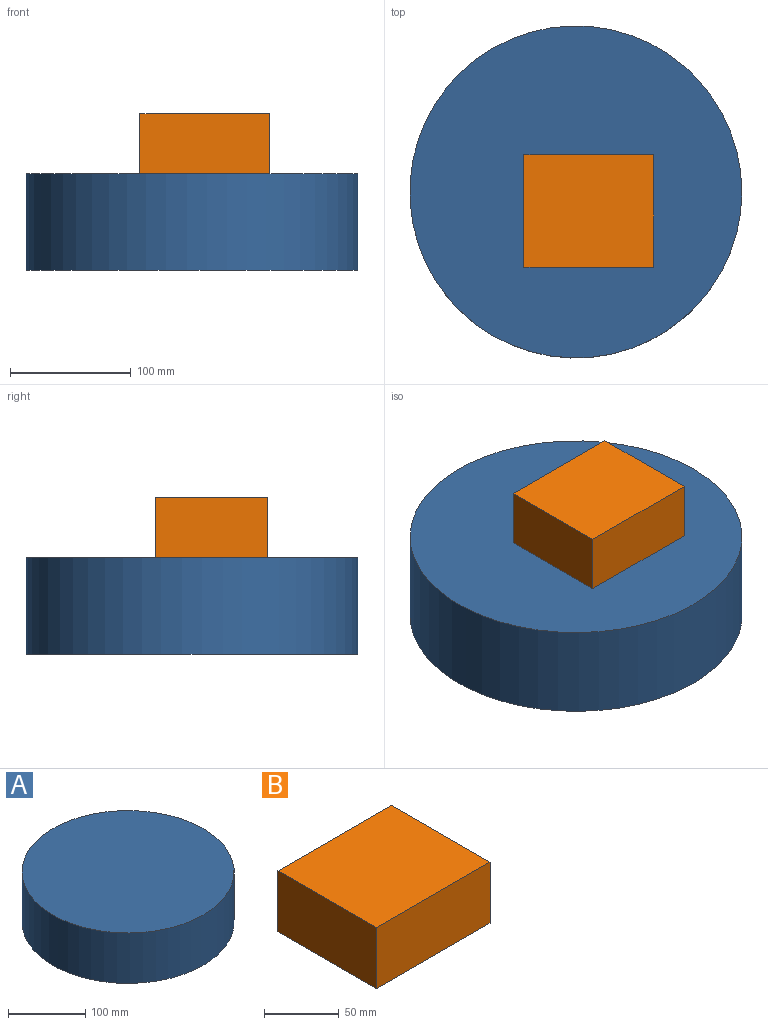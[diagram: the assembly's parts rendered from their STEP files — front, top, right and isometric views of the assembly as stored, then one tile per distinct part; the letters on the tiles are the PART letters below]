
ASSEMBLY  parts=2 mates=1
PART A: 3 faces, bbox 275.2x275.2x80 mm
  f0: cylinder r=137.62mm len=275.23mm, axis (0,0,1), area 69173.8mm2, adj f1,f2
  f1: plane 275.23x275.23mm, normal (0,0,-1), area 59496.8mm2, adj f0
  f2: plane 275.23x275.23mm, normal (0,0,1), area 59496.8mm2, adj f0
PART B: 6 faces, bbox 107.4x93.1x50 mm
  f0: plane 107.43x50mm, normal (0,1,0), area 5371.7mm2, adj f1,f3,f4,f5
  f1: plane 93.09x50mm, normal (-1,0,0), area 4654.6mm2, adj f0,f2,f4,f5
  f2: plane 107.43x50mm, normal (0,-1,0), area 5371.7mm2, adj f1,f3,f4,f5
  f3: plane 93.09x50mm, normal (1,0,0), area 4654.6mm2, adj f0,f2,f4,f5
  f4: plane 107.43x93.09mm, normal (0,0,1), area 10001.2mm2, adj f0,f1,f2,f3
  f5: plane 107.43x93.09mm, normal (0,0,-1), area 10001.2mm2, adj f0,f1,f2,f3
PLACE A t=(-8.08,-48.3,50.75)mm
PLACE B t=(-241.49,-61.07,55.75)mm
MATE planar A.f0 <-> B.f5  axis (0,0,1) through (-247.91,-48.3,55.75)mm
